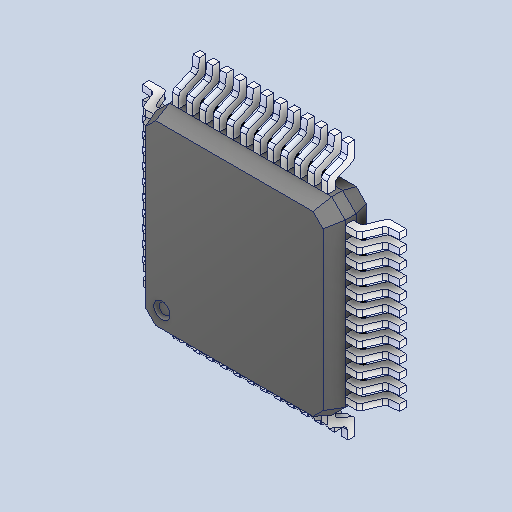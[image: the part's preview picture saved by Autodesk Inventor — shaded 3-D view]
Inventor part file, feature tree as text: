
AUTODESK INVENTOR PART (.ipt)
format: ipt  version: 2024 (Build 280153000, 153)  size: 605,184 bytes
history: native  units: mm
features: chamfer x1
ambient origin geometry x8: Origin, YZ Plane, XZ Plane, XY Plane, X Axis, Y Axis, Z Axis, Center Point
bodies: Solid1 (feature_tree)
feature tree (1):
  chamfer  "Chamfer4"  [1 undecoded]
note: 1 required parameter value undecoded (feature->parameter linkage not recoverable at this tier; creation-order binding heuristic only, values carry confidence <= 0.55)
